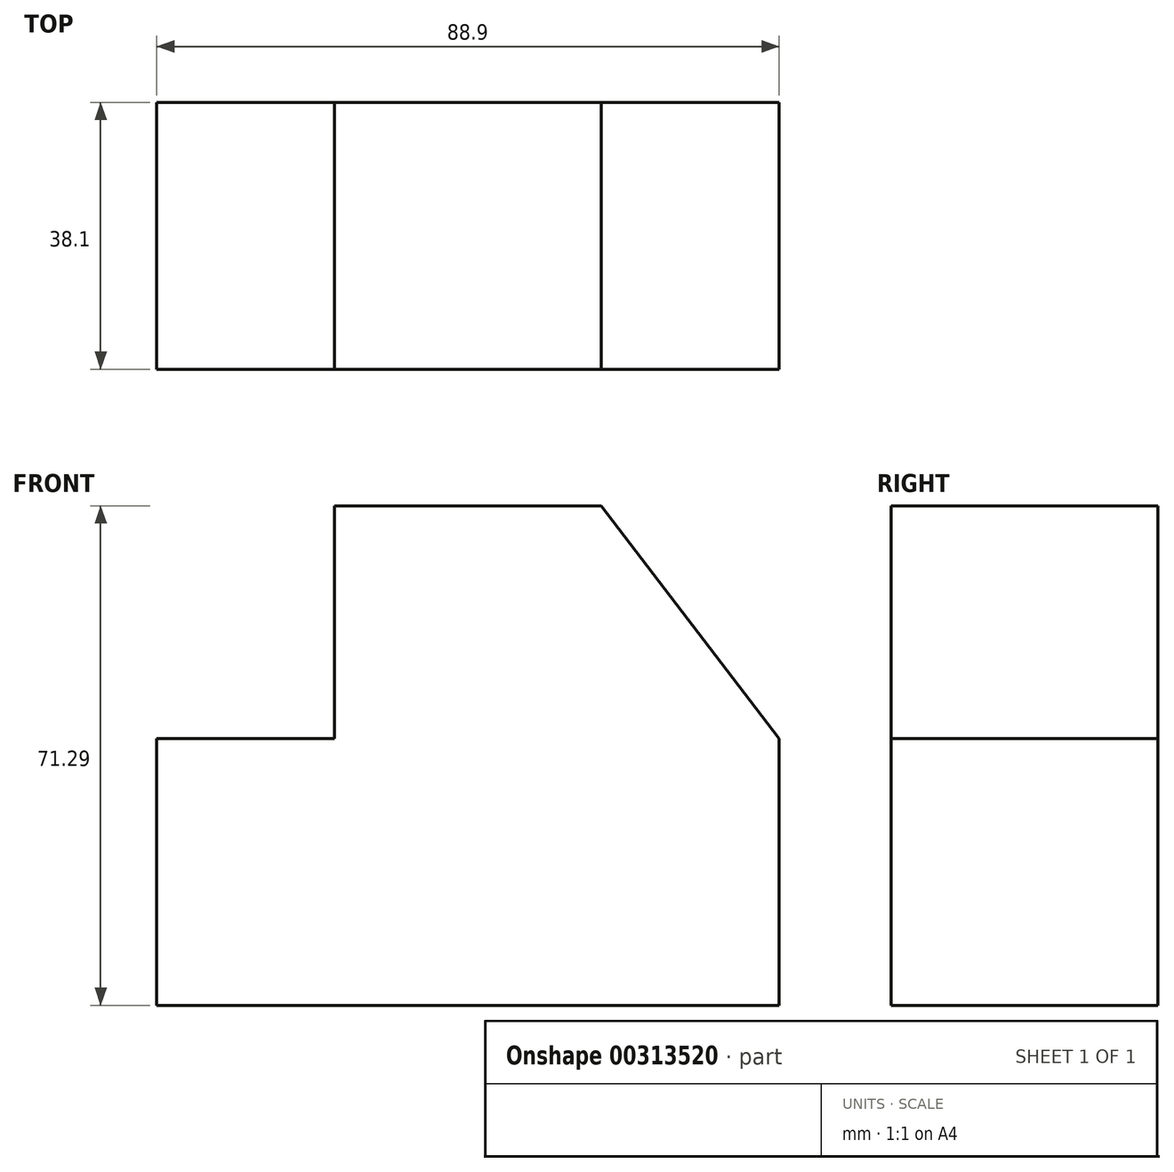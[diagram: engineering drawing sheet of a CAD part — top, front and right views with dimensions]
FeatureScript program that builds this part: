
annotation { "Feature Type Name" : "Feature", "Feature Type Description" : "" }
export const myFeature = defineFeature(function(context is Context, id is Id, definition is map)
    precondition{}
    {
        {
            var Q0;
            Q0=qCreatedBy(makeId("Front.planeOp"),FACE);
            var sketch = newSketch(context, id + "F0", { "sketchPlane" : qUnion([Q0])});
            skLineSegment(sketch, "E0", {"start": v(-51.47, -0.3) * mm, "end": v(-51.47, -38.4) * mm});
            skLineSegment(sketch, "E1", {"start": v(-51.47, -38.4) * mm, "end": v(37.43, -38.4) * mm});
            skLineSegment(sketch, "E2", {"start": v(37.43, -38.4) * mm, "end": v(37.43, -0.3) * mm});
            skLineSegment(sketch, "E3", {"start": v(37.43, -0.3) * mm, "end": v(12.03, 32.89) * mm});
            skLineSegment(sketch, "E4", {"start": v(12.03, 32.89) * mm, "end": v(-26.07, 32.89) * mm});
            skLineSegment(sketch, "E5", {"start": v(-26.07, 32.89) * mm, "end": v(-26.07, -0.3) * mm});
            skLineSegment(sketch, "E6", {"start": v(-26.07, -0.3) * mm, "end": v(-51.47, -0.3) * mm});
            skSolve(sketch);
        }
        {
            var Q0;
            Q0=makeQuery(id+"F0.imprint","IMPRINT",FACE,{"disambiguationData":[TD([[makeQuery(id+"F0.imprint","IMPRINT",EDGE,{"derivedFrom":sQuery(id+"F0.wireOp",EDGE,"E0")}),1.0]])]});
            extrude(context, id + "F1", {"entities" : qUnion([Q0]), "depth" : 38.1 * mm});
        }
    });
